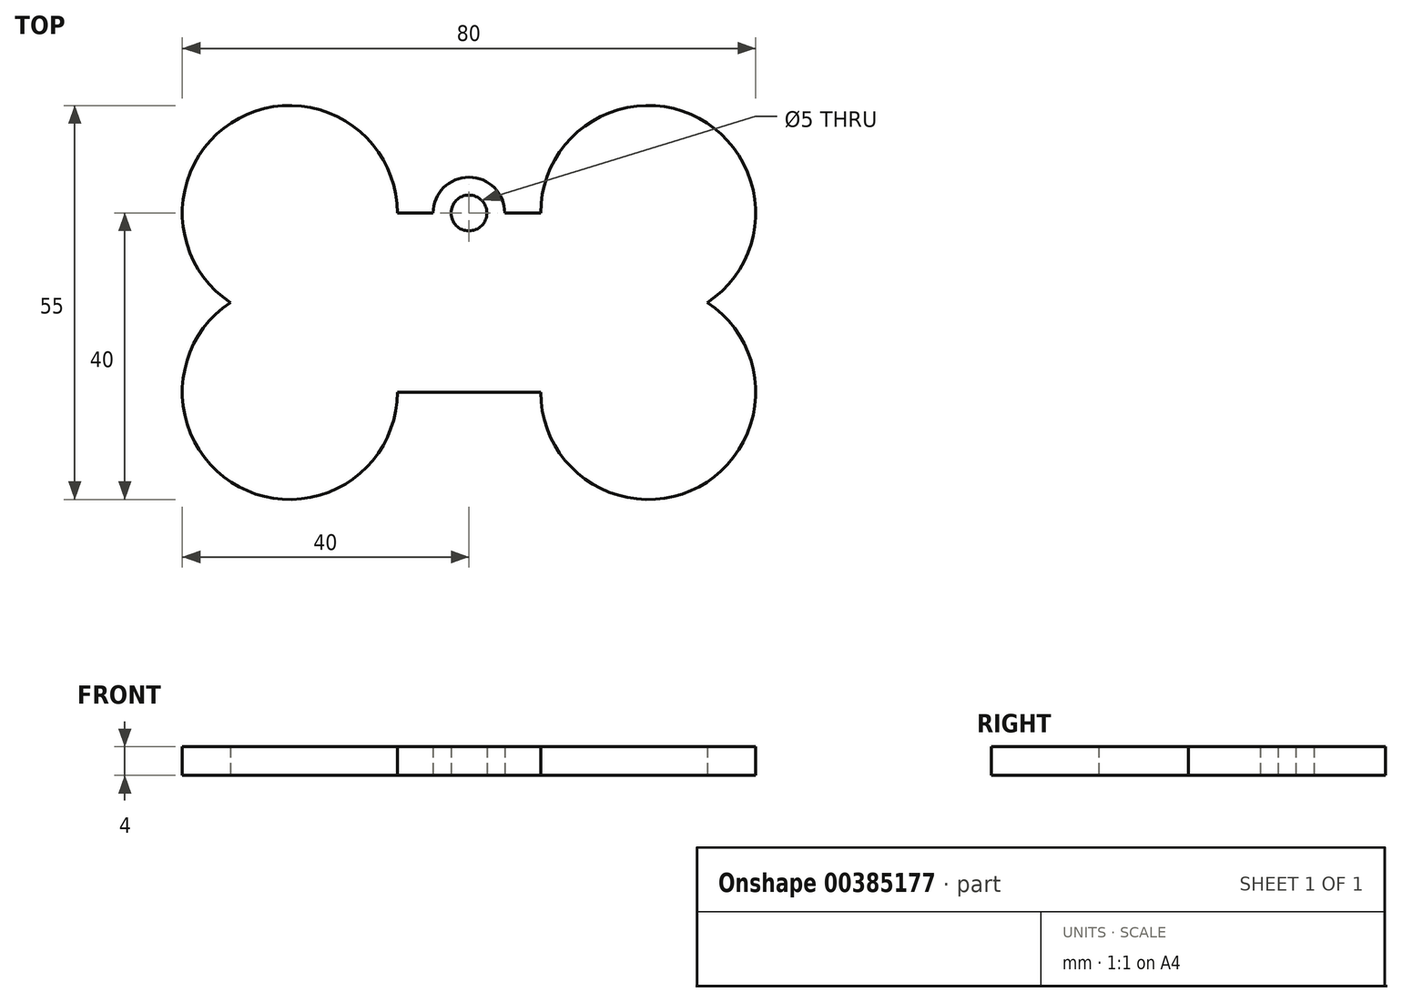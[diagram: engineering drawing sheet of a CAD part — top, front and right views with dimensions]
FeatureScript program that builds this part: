
annotation { "Feature Type Name" : "Feature", "Feature Type Description" : "" }
export const myFeature = defineFeature(function(context is Context, id is Id, definition is map)
    precondition{}
    {
        {
            var Q0;
            Q0=qCreatedBy(makeId("Top.planeOp"),FACE);
            var sketch = newSketch(context, id + "F0", { "sketchPlane" : qUnion([Q0])});
            skLineSegment(sketch, "E0.bottom", {"start": v(-10, 12.5) * mm, "end": v(-5, 12.5) * mm});
            skLineSegment(sketch, "E0.top", {"start": v(-10, -12.5) * mm, "end": v(10, -12.5) * mm});
            skArc(sketch, "E1", {"start": v(-10, 12.5) * mm, "mid": v(-32.1, 25.72) * mm, "end": v(-33.3, 0) * mm});
            skArc(sketch, "E2", {"start": v(-33.3, 0) * mm, "mid": v(-32.1, -25.72) * mm, "end": v(-10, -12.5) * mm});
            skArc(sketch, "E3", {"start": v(33.3, 0) * mm, "mid": v(32.1, 25.72) * mm, "end": v(10, 12.5) * mm});
            skArc(sketch, "E4", {"start": v(10, -12.5) * mm, "mid": v(32.1, -25.72) * mm, "end": v(33.3, 0) * mm});
            skArc(sketch, "E5", {"start": v(5, 12.5) * mm, "mid": v(0, 17.5) * mm, "end": v(-5, 12.5) * mm});
            skCircle(sketch, "E6", {"center": v(0, 12.5) * mm, "radius": 2.5 * mm});
            skLineSegment(sketch, "E7.trimOffspring", {"start": v(5, 12.5) * mm, "end": v(10, 12.5) * mm});
            skSolve(sketch);
        }
        {
            var Q0;
            Q0=makeQuery(id+"F0.imprint","IMPRINT",FACE,{"disambiguationData":[TD([[makeQuery(id+"F0.imprint","IMPRINT",EDGE,{"derivedFrom":sQuery(id+"F0.wireOp",EDGE,"E0.bottom")}),-1.0]])]});
            extrude(context, id + "F1", {"entities" : qUnion([Q0]), "depth" : 4 * mm});
        }
    });
